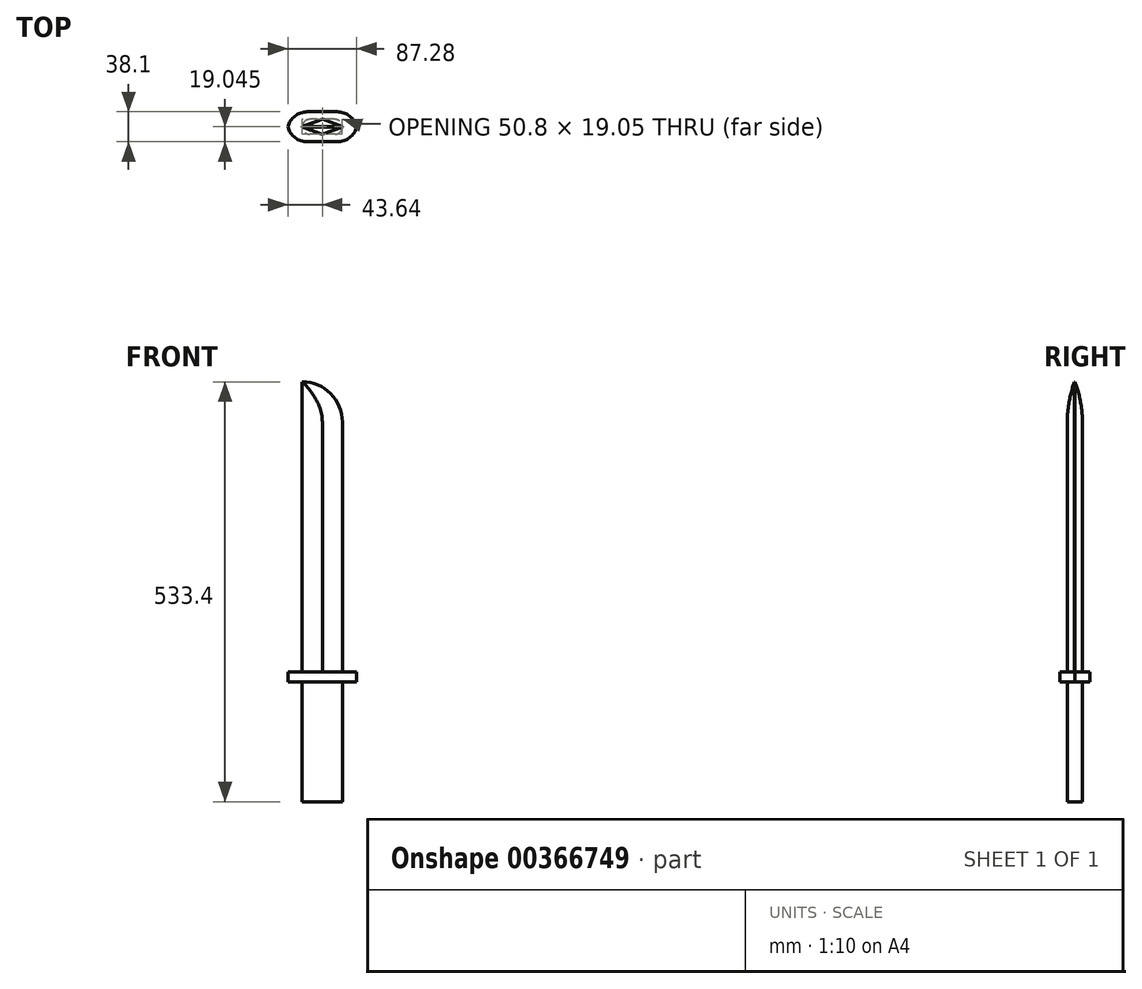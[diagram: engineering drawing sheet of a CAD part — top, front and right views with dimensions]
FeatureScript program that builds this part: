
annotation { "Feature Type Name" : "Feature", "Feature Type Description" : "" }
export const myFeature = defineFeature(function(context is Context, id is Id, definition is map)
    precondition{}
    {
        {
            var Q0;
            Q0=qCreatedBy(makeId("Front.planeOp"),FACE);
            var sketch = newSketch(context, id + "F0", { "sketchPlane" : qUnion([Q0])});
            skLineSegment(sketch, "E0", {"start": v(0, -86.24) * mm, "end": v(25.4, -86.24) * mm});
            skLineSegment(sketch, "E1", {"start": v(25.4, -86.24) * mm, "end": v(25.4, 66.16) * mm});
            skLineSegment(sketch, "E2.MirrorCS", {"start": v(-25.4, -86.24) * mm, "end": v(-25.4, 66.16) * mm});
            skLineSegment(sketch, "E3.MirrorCS", {"start": v(0, -86.24) * mm, "end": v(-25.4, -86.24) * mm});
            skLineSegment(sketch, "E4", {"start": v(-25.4, 66.16) * mm, "end": v(25.4, 66.16) * mm});
            skSolve(sketch);
        }
        {
            var Q0;
            Q0 = qSketchRegion(id + "F0", true);
            extrude(context, id + "F1", {"entities" : qUnion([Q0]), "depth" : 19.05 * mm});
        }
        {
            var Q0;
            Q0=makeQuery(id+"F1.opExtrude","SWEPT_FACE",FACE,{"disambiguationData":[OSD([sQuery(id+"F0.wireOp",EDGE,"E4")])]});
            var sketch = newSketch(context, id + "F2", { "sketchPlane" : qUnion([Q0])});
            skLineSegment(sketch, "E5", {"start": v(0, 0) * mm, "end": v(0, -19.05) * mm});
            skLineSegment(sketch, "E6", {"start": v(0, -19.05) * mm, "end": v(0, -9.53) * mm});
            skLineSegment(sketch, "E7.bottom", {"start": v(44.45, -28.58) * mm, "end": v(-44.45, -28.58) * mm});
            skLineSegment(sketch, "E7.top", {"start": v(44.45, 9.53) * mm, "end": v(-44.45, 9.53) * mm});
            skLineSegment(sketch, "E7.left", {"start": v(44.45, -28.58) * mm, "end": v(44.45, 9.53) * mm});
            skLineSegment(sketch, "E7.right", {"start": v(-44.45, -28.58) * mm, "end": v(-44.45, 9.53) * mm});
            skPoint(sketch, "E7.middle", {"position": v(0, -9.53) * mm});
            skSolve(sketch);
        }
        {
            var Q0;
            Q0 = qSketchRegion(id + "F2", true);
            extrude(context, id + "F3", {"entities" : qUnion([Q0]), "operationType" : NewBodyOperationType.ADD, "depth" : 12.7 * mm});
        }
        {
            var Q0;
            Q0=makeQuery(id+"F1.opExtrude","CAP_FACE",FACE,{"disambiguationData":[OSD([sQuery(id+"F0.wireOp",EDGE,"E0"),sQuery(id+"F0.wireOp",EDGE,"E1"),sQuery(id+"F0.wireOp",EDGE,"E2.MirrorCS"),sQuery(id+"F0.wireOp",EDGE,"E3.MirrorCS"),sQuery(id+"F0.wireOp",EDGE,"E4")])],"isStart":true});
            var sketch = newSketch(context, id + "F4", { "sketchPlane" : qUnion([Q0])});
            skLineSegment(sketch, "E8", {"start": v(-25.4, 66.16) * mm, "end": v(-25.4, 447.16) * mm});
            skLineSegment(sketch, "E9", {"start": v(25.4, 66.16) * mm, "end": v(25.4, 447.16) * mm});
            skLineSegment(sketch, "E10", {"start": v(-25.4, 447.16) * mm, "end": v(25.4, 447.16) * mm});
            skSolve(sketch);
        }
        {
            var Q0;
            Q0=makeQuery(id+"F4.imprint","IMPRINT",FACE,{"disambiguationData":[TD([[makeQuery(id+"F4.imprint","IMPRINT",EDGE,{"derivedFrom":sQuery(id+"F4.wireOp",EDGE,"E8")}),-1.0]])]});
            extrude(context, id + "F5", {"entities" : qUnion([Q0]), "operationType" : NewBodyOperationType.ADD, "depth" : -19.05 * mm});
        }
        {
            var Q0;
            Q0=makeQuery(id+"F5.opExtrude","SWEPT_EDGE",EDGE,{"disambiguationData":[OSD([sQuery(id+"F4.wireOp",EDGE,"E8"),sQuery(id+"F4.wireOp",EDGE,"E10")])]});
            fillet(context, id + "F6", {"entities" : qUnion([Q0]), "radius" : 50.8 * mm, "tangentPropagation" : true, "allowEdgeOverflow" : false});
        }
        {
            var Q0;
            Q0=makeQuery(id+"F5.opExtrude","CAP_EDGE",EDGE,{"disambiguationData":[OSD([sQuery(id+"F4.wireOp",EDGE,"E9")])],"isStart":true});
            var Q1;
            Q1=makeQuery(id+"F5.opExtrude","CAP_EDGE",EDGE,{"disambiguationData":[OSD([sQuery(id+"F4.wireOp",EDGE,"E9")])],"isStart":false});
            var Q2;
            Q2=makeQuery(id+"F5.opExtrude","CAP_EDGE",EDGE,{"disambiguationData":[OSD([sQuery(id+"F4.wireOp",EDGE,"E8")])],"isStart":true});
            var Q3;
            Q3=makeQuery(id+"F5.opExtrude","CAP_EDGE",EDGE,{"disambiguationData":[OSD([sQuery(id+"F4.wireOp",EDGE,"E8")])],"isStart":false});
            var Q4;
            {var subQ0=sQuery(id+"F4.wireOp",EDGE,"E10");var subQ1=sQuery(id+"F4.wireOp",EDGE,"E8");Q4=makeQuery(id+"F6.opFillet","BLEND_EDGE",EDGE,{"blendedFrom":[makeQuery(id+"F5.opExtrude","SWEPT_EDGE",EDGE,{"disambiguationData":[OSD([subQ1,subQ0])]}),makeQuery(id+"F5.opExtrude","CAP_FACE",FACE,{"disambiguationData":[OSD([sQuery(id+"F0.wireOp",EDGE,"E4"),subQ1,sQuery(id+"F4.wireOp",EDGE,"E9"),subQ0])],"isStart":true})],"blendedInto":[makeQuery(id+"F5.opExtrude","CAP_FACE",FACE,{"disambiguationData":[OSD([sQuery(id+"F0.wireOp",EDGE,"E4"),subQ1,sQuery(id+"F4.wireOp",EDGE,"E9"),subQ0])],"isStart":true})]});}
            var Q5;
            {var subQ0=sQuery(id+"F4.wireOp",EDGE,"E10");var subQ1=sQuery(id+"F4.wireOp",EDGE,"E8");Q5=makeQuery(id+"F6.opFillet","BLEND_EDGE",EDGE,{"blendedFrom":[makeQuery(id+"F5.opExtrude","SWEPT_EDGE",EDGE,{"disambiguationData":[OSD([subQ1,subQ0])]}),makeQuery(id+"F5.opExtrude","CAP_FACE",FACE,{"disambiguationData":[OSD([sQuery(id+"F0.wireOp",EDGE,"E4"),subQ1,sQuery(id+"F4.wireOp",EDGE,"E9"),subQ0])],"isStart":false})],"blendedInto":[makeQuery(id+"F5.opExtrude","CAP_FACE",FACE,{"disambiguationData":[OSD([sQuery(id+"F0.wireOp",EDGE,"E4"),subQ1,sQuery(id+"F4.wireOp",EDGE,"E9"),subQ0])],"isStart":false})]});}
            chamfer(context, id + "F7", {"entities" : qUnion([Q0, Q1, Q2, Q3, Q4, Q5]), "chamferType" : ChamferType.OFFSET_ANGLE, "width" : 25.4 * mm, "oppositeDirection" : false, "angle" : 20 * degree, "tangentPropagation" : true});
        }
        {
            var Q0;
            Q0=makeQuery(id+"F1.opExtrude","CAP_EDGE",EDGE,{"disambiguationData":[OSD([sQuery(id+"F0.wireOp",EDGE,"E1")])],"isStart":true});
            var Q1;
            Q1=makeQuery(id+"F1.opExtrude","CAP_EDGE",EDGE,{"disambiguationData":[OSD([sQuery(id+"F0.wireOp",EDGE,"E2.MirrorCS")])],"isStart":true});
            var Q2;
            Q2=makeQuery(id+"F1.opExtrude","CAP_EDGE",EDGE,{"disambiguationData":[OSD([sQuery(id+"F0.wireOp",EDGE,"E2.MirrorCS")])],"isStart":false});
            var Q3;
            Q3=makeQuery(id+"F1.opExtrude","CAP_EDGE",EDGE,{"disambiguationData":[OSD([sQuery(id+"F0.wireOp",EDGE,"E1")])],"isStart":false});
            fillet(context, id + "F8", {"entities" : qUnion([Q0, Q1, Q2, Q3]), "radius" : 9.52 * mm, "tangentPropagation" : true, "allowEdgeOverflow" : false});
        }
        {
            var Q0;
            Q0=makeQuery(id+"F3.opExtrude","SWEPT_EDGE",EDGE,{"disambiguationData":[OSD([sQuery(id+"F2.wireOp",EDGE,"E7.bottom"),sQuery(id+"F2.wireOp",EDGE,"E7.left")])]});
            var Q1;
            Q1=makeQuery(id+"F3.opExtrude","SWEPT_EDGE",EDGE,{"disambiguationData":[OSD([sQuery(id+"F2.wireOp",EDGE,"E7.top"),sQuery(id+"F2.wireOp",EDGE,"E7.left")])]});
            var Q2;
            Q2=makeQuery(id+"F3.opExtrude","SWEPT_EDGE",EDGE,{"disambiguationData":[OSD([sQuery(id+"F2.wireOp",EDGE,"E7.bottom"),sQuery(id+"F2.wireOp",EDGE,"E7.right")])]});
            var Q3;
            Q3=makeQuery(id+"F3.opExtrude","SWEPT_EDGE",EDGE,{"disambiguationData":[OSD([sQuery(id+"F2.wireOp",EDGE,"E7.top"),sQuery(id+"F2.wireOp",EDGE,"E7.right")])]});
            fillet(context, id + "F9", {"entities" : qUnion([Q0, Q1, Q2, Q3]), "radius" : 25.4 * mm, "tangentPropagation" : true, "allowEdgeOverflow" : false});
        }
    });
